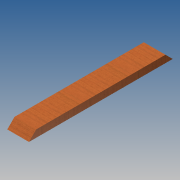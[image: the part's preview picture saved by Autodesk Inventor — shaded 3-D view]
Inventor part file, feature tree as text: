
AUTODESK INVENTOR PART (.ipt)
format: ipt  version: 2014 SP1 (Build 180222100, 222)  size: 91,648 bytes
history: native  units: in
note: dims shown in document units (in); Inventor stores cm internally (conversion verified against a paired STEP export)
features: sketch x2, extrude x1, hole x1
ambient origin geometry x8: Origin, YZ Plane, XZ Plane, XY Plane, X Axis, Y Axis, Z Axis, Center Point
bodies: Solid1 (feature_tree)
feature tree (4):
  extrude  "Extrusion1"  Depth=4.4882in TaperAngle=0.0deg
  hole  "Hole1"  [1 undecoded]
  sketch  "Sketch1"  dims[d2=45.0deg d3=4.4882in d4=0.0in]
  sketch  "Sketch2"  dims[d5=1.122in d6=0.7874in d8=2.2441in d9=0.3937in d11=1.0in d13=0.25in d14=0.75in d15=0.375in d16=0.25in d17=0.5635in d18=1.0in d19=0.8108in d20=29.75in]
note: 1 required parameter value undecoded (feature->parameter linkage not recoverable at this tier; creation-order binding heuristic only, values carry confidence <= 0.55)
